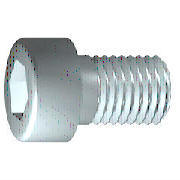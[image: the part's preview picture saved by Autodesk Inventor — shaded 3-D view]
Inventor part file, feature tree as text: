
AUTODESK INVENTOR PART (.ipt)
format: ipt  version: 2020 (Build 240168000, 168)  size: 194,560 bytes
history: native  units: mm (DEFAULTED — no unit token found)
features: sketch x2, other x1, extrude x1, plane x1, fillet x1
ambient origin geometry x7: Origin, YZ Plane, XY Plane, X Axis, Y Axis, Z Axis, Center Point
bodies: Solid1 (feature_tree)
feature tree (6):
  other  "Bryła"
  extrude  "Szczelina"  Depth=22.0mm
  plane  "Work Plane1"
  fillet  "Fillet2"  Radius=0.61355mm
  sketch  "Szkic1"
  sketch  "Szkic2"
